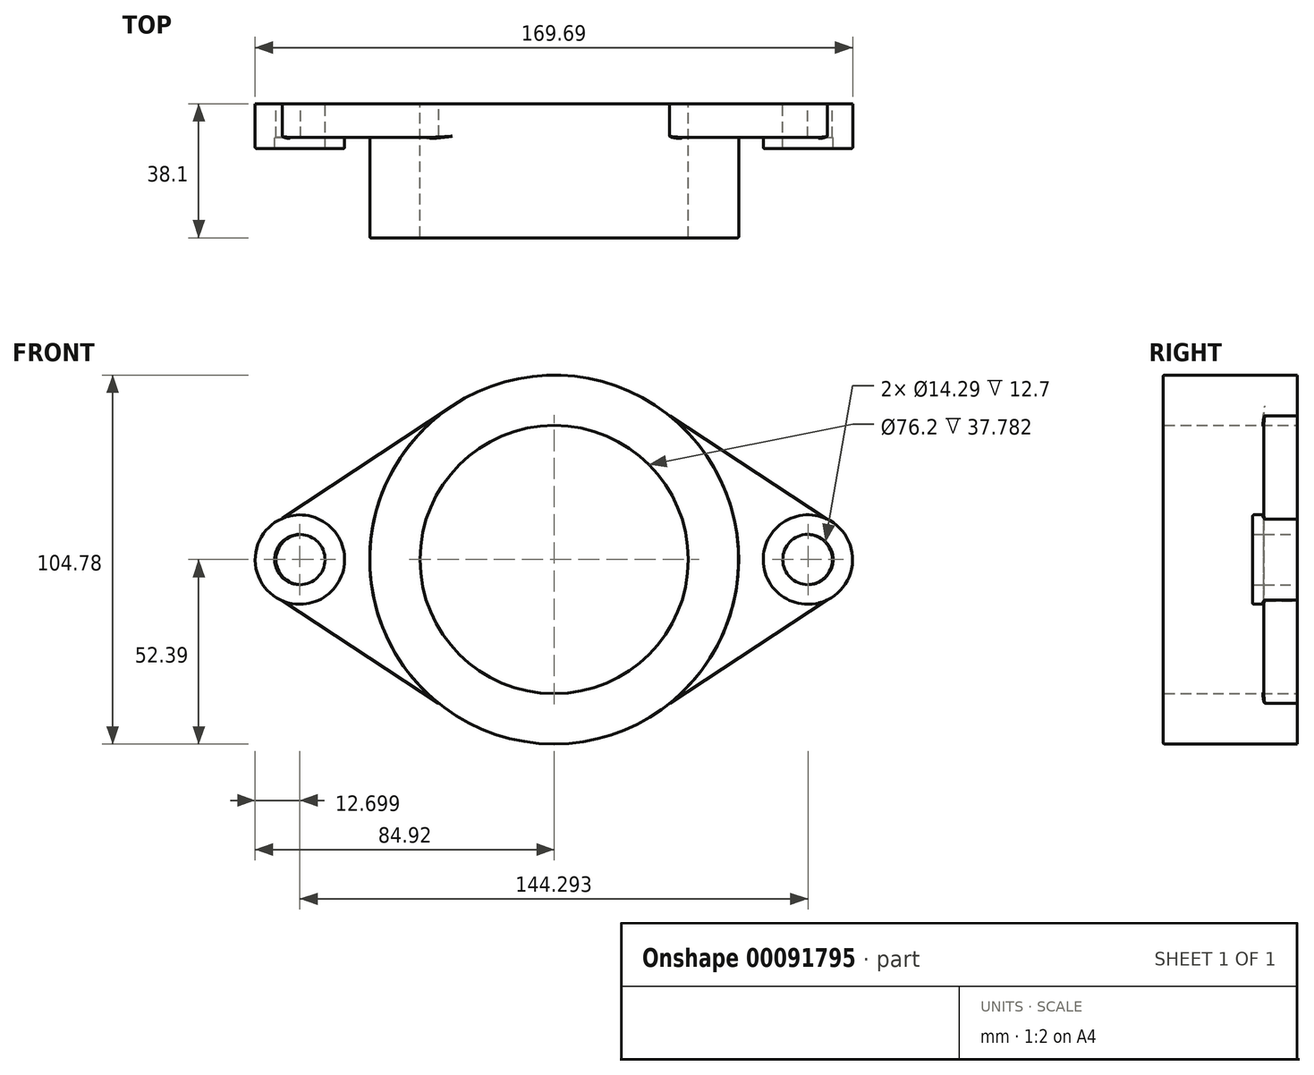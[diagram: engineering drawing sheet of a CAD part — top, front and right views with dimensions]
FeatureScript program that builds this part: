
annotation { "Feature Type Name" : "Feature", "Feature Type Description" : "" }
export const myFeature = defineFeature(function(context is Context, id is Id, definition is map)
    precondition{}
    {
        {
            var Q0;
            Q0=qCreatedBy(makeId("Front.planeOp"),FACE);
            var sketch = newSketch(context, id + "F0", { "sketchPlane" : qUnion([Q0])});
            skCircle(sketch, "E0", {"center": v(0, 0) * mm, "radius": 38.1 * mm});
            skCircle(sketch, "E1", {"center": v(-71.83, 0) * mm, "radius": 7.14 * mm});
            skCircle(sketch, "E2", {"center": v(71.86, 0) * mm, "radius": 7.14 * mm});
            skCircle(sketch, "E3", {"center": v(0, 0) * mm, "radius": 52.39 * mm});
            skCircle(sketch, "E4", {"center": v(71.86, 0) * mm, "radius": 12.7 * mm});
            skLineSegment(sketch, "E5", {"start": v(78.94, 10.54) * mm, "end": v(32.82, 40.84) * mm});
            skLineSegment(sketch, "E6", {"start": v(78.94, -10.54) * mm, "end": v(32.82, -40.84) * mm});
            skCircle(sketch, "E7", {"center": v(-71.83, 0) * mm, "radius": 12.7 * mm});
            skLineSegment(sketch, "E8", {"start": v(0, 75.6) * mm, "end": v(0, 106.25) * mm});
            skLineSegment(sketch, "E9", {"start": v(-78.94, 10.52) * mm, "end": v(-28.95, 43.67) * mm});
            skLineSegment(sketch, "E10", {"start": v(-78.94, -10.52) * mm, "end": v(-32.82, -40.84) * mm});
            skArc(sketch, "E11", {"start": v(-78.94, -10.52) * mm, "mid": v(-84.53, 0.11) * mm, "end": v(-78.75, 10.65) * mm});
            skArc(sketch, "E12", {"start": v(78.94, -10.54) * mm, "mid": v(84.56, 0) * mm, "end": v(78.94, 10.54) * mm});
            skArc(sketch, "E13", {"start": v(-28.95, 43.67) * mm, "mid": v(2.4, 52.33) * mm, "end": v(32.82, 40.84) * mm});
            skArc(sketch, "E14", {"start": v(-32.82, -40.84) * mm, "mid": v(0, -52.39) * mm, "end": v(32.82, -40.84) * mm});
            skSolve(sketch);
        }
        {
            var Q0;
            Q0 = qSketchRegion(id + "F0", true);
            extrude(context, id + "F1", {"entities" : qUnion([Q0]), "depth" : 9.52 * mm});
        }
        {
            var Q0;
            Q0=qCreatedBy(makeId("Front.planeOp"),FACE);
            var sketch = newSketch(context, id + "F2", { "sketchPlane" : qUnion([Q0])});
            skCircle(sketch, "E15", {"center": v(72.07, 0) * mm, "radius": 12.7 * mm});
            skCircle(sketch, "E16", {"center": v(-72.22, 0) * mm, "radius": 12.7 * mm});
            skCircle(sketch, "E17", {"center": v(0, 0) * mm, "radius": 52.39 * mm});
            skCircle(sketch, "E18", {"center": v(0, 0) * mm, "radius": 38.1 * mm});
            skCircle(sketch, "E19", {"center": v(-72.22, 0) * mm, "radius": 7.14 * mm});
            skCircle(sketch, "E20", {"center": v(72.07, 0) * mm, "radius": 7.14 * mm});
            skSolve(sketch);
        }
        {
            var Q0;
            Q0=makeQuery(id+"F2.imprint","IMPRINT",FACE,{"disambiguationData":[TD([[makeQuery(id+"F2.imprint","IMPRINT",EDGE,{"derivedFrom":sQuery(id+"F2.wireOp",EDGE,"E15")}),1.0]])]});
            var Q1;
            Q1=makeQuery(id+"F2.imprint","IMPRINT",FACE,{"disambiguationData":[TD([[makeQuery(id+"F2.imprint","IMPRINT",EDGE,{"derivedFrom":sQuery(id+"F2.wireOp",EDGE,"E16")}),1.0]])]});
            var Q2;
            Q2=makeQuery(id+"F2.imprint","IMPRINT",FACE,{"disambiguationData":[TD([[makeQuery(id+"F2.imprint","IMPRINT",EDGE,{"derivedFrom":sQuery(id+"F2.wireOp",EDGE,"E17")}),1.0]])]});
            extrude(context, id + "F3", {"entities" : qUnion([Q0, Q1, Q2]), "operationType" : NewBodyOperationType.ADD, "depth" : 12.7 * mm});
        }
        {
            var Q0;
            Q0=qCreatedBy(makeId("Front.planeOp"),FACE);
            var sketch = newSketch(context, id + "F4", { "sketchPlane" : qUnion([Q0])});
            skCircle(sketch, "E21", {"center": v(0, 0) * mm, "radius": 52.39 * mm});
            skCircle(sketch, "E22", {"center": v(0, 0) * mm, "radius": 38.1 * mm});
            skSolve(sketch);
        }
        {
            var Q0;
            Q0 = qSketchRegion(id + "F4", true);
            extrude(context, id + "F5", {"entities" : qUnion([Q0]), "operationType" : NewBodyOperationType.ADD, "depth" : 38.1 * mm});
        }
        {
            var Q0;
            Q0=makeQuery(id+"F5.opExtrude","CAP_EDGE",EDGE,{"disambiguationData":[OSD([sQuery(id+"F4.wireOp",EDGE,"E21")])],"isStart":false});
            var Q1;
            Q1=makeQuery(id+"F5.opExtrude","CAP_EDGE",EDGE,{"disambiguationData":[OSD([sQuery(id+"F4.wireOp",EDGE,"E22")])],"isStart":false});
            var Q2;
            Q2=makeQuery(id+"F3.opExtrude","CAP_EDGE",EDGE,{"disambiguationData":[OSD([sQuery(id+"F2.wireOp",EDGE,"E15")])],"isStart":false});
            var Q3;
            Q3=makeQuery(id+"F3.boolean.opBoolean","INTERSECT",EDGE,{"derivedFrom":[makeQuery(id+"F1.opExtrude","CAP_FACE",FACE,{"disambiguationData":[OSD([sQuery(id+"F0.wireOp",EDGE,"E0"),sQuery(id+"F0.wireOp",EDGE,"E1"),sQuery(id+"F0.wireOp",EDGE,"E2"),sQuery(id+"F0.wireOp",EDGE,"E3"),sQuery(id+"F0.wireOp",EDGE,"E4"),sQuery(id+"F0.wireOp",EDGE,"E5"),sQuery(id+"F0.wireOp",EDGE,"E6"),sQuery(id+"F0.wireOp",EDGE,"E7"),sQuery(id+"F0.wireOp",EDGE,"E9"),sQuery(id+"F0.wireOp",EDGE,"E10")])],"isStart":false}),makeQuery(id+"F3.opExtrude","SWEPT_FACE",FACE,{"disambiguationData":[OSD([sQuery(id+"F2.wireOp",EDGE,"E15")])]})]});
            var Q4;
            Q4=makeQuery(id+"F3.opExtrude","CAP_EDGE",EDGE,{"disambiguationData":[OSD([sQuery(id+"F2.wireOp",EDGE,"E16")])],"isStart":false});
            var Q5;
            Q5=makeQuery(id+"F3.boolean.opBoolean","INTERSECT",EDGE,{"derivedFrom":[makeQuery(id+"F1.opExtrude","CAP_FACE",FACE,{"disambiguationData":[OSD([sQuery(id+"F0.wireOp",EDGE,"E0"),sQuery(id+"F0.wireOp",EDGE,"E1"),sQuery(id+"F0.wireOp",EDGE,"E2"),sQuery(id+"F0.wireOp",EDGE,"E3"),sQuery(id+"F0.wireOp",EDGE,"E4"),sQuery(id+"F0.wireOp",EDGE,"E5"),sQuery(id+"F0.wireOp",EDGE,"E6"),sQuery(id+"F0.wireOp",EDGE,"E7"),sQuery(id+"F0.wireOp",EDGE,"E9"),sQuery(id+"F0.wireOp",EDGE,"E10")])],"isStart":false}),makeQuery(id+"F3.opExtrude","SWEPT_FACE",FACE,{"disambiguationData":[OSD([sQuery(id+"F2.wireOp",EDGE,"E16")])]})]});
            var Q6;
            Q6=makeQuery(id+"F3.boolean.opBoolean","INTERSECT",EDGE,{"disambiguationData":[OD(1.0)],"derivedFrom":[makeQuery(id+"F1.opExtrude","CAP_FACE",FACE,{"disambiguationData":[OSD([sQuery(id+"F0.wireOp",EDGE,"E0"),sQuery(id+"F0.wireOp",EDGE,"E1"),sQuery(id+"F0.wireOp",EDGE,"E2"),sQuery(id+"F0.wireOp",EDGE,"E3"),sQuery(id+"F0.wireOp",EDGE,"E4"),sQuery(id+"F0.wireOp",EDGE,"E5"),sQuery(id+"F0.wireOp",EDGE,"E6"),sQuery(id+"F0.wireOp",EDGE,"E7"),sQuery(id+"F0.wireOp",EDGE,"E9"),sQuery(id+"F0.wireOp",EDGE,"E10")])],"isStart":false}),makeQuery(id+"F3.opExtrude","SWEPT_FACE",FACE,{"disambiguationData":[OSD([sQuery(id+"F2.wireOp",EDGE,"E17")])]})]});
            var Q7;
            Q7=makeQuery(id+"F1.opExtrude","CAP_EDGE",EDGE,{"disambiguationData":[OSD([sQuery(id+"F0.wireOp",EDGE,"E10")])],"isStart":false});
            var Q8;
            Q8=makeQuery(id+"F1.opExtrude","CAP_EDGE",EDGE,{"disambiguationData":[OSD([sQuery(id+"F0.wireOp",EDGE,"E9")])],"isStart":false});
            var Q9;
            Q9=makeQuery(id+"F3.boolean.opBoolean","INTERSECT",EDGE,{"disambiguationData":[OD(0.0)],"derivedFrom":[makeQuery(id+"F1.opExtrude","CAP_FACE",FACE,{"disambiguationData":[OSD([sQuery(id+"F0.wireOp",EDGE,"E0"),sQuery(id+"F0.wireOp",EDGE,"E1"),sQuery(id+"F0.wireOp",EDGE,"E2"),sQuery(id+"F0.wireOp",EDGE,"E3"),sQuery(id+"F0.wireOp",EDGE,"E4"),sQuery(id+"F0.wireOp",EDGE,"E5"),sQuery(id+"F0.wireOp",EDGE,"E6"),sQuery(id+"F0.wireOp",EDGE,"E7"),sQuery(id+"F0.wireOp",EDGE,"E9"),sQuery(id+"F0.wireOp",EDGE,"E10")])],"isStart":false}),makeQuery(id+"F3.opExtrude","SWEPT_FACE",FACE,{"disambiguationData":[OSD([sQuery(id+"F2.wireOp",EDGE,"E17")])]})]});
            var Q10;
            Q10=makeQuery(id+"F1.opExtrude","CAP_EDGE",EDGE,{"disambiguationData":[OSD([sQuery(id+"F0.wireOp",EDGE,"E6")])],"isStart":false});
            var Q11;
            Q11=makeQuery(id+"F1.opExtrude","CAP_EDGE",EDGE,{"disambiguationData":[OSD([sQuery(id+"F0.wireOp",EDGE,"E5")])],"isStart":false});
            fillet(context, id + "F6", {"entities" : qUnion([Q0, Q1, Q2, Q3, Q4, Q5, Q6, Q7, Q8, Q9, Q10, Q11]), "radius" : 0.32 * mm, "tangentPropagation" : true, "allowEdgeOverflow" : false});
        }
    });
